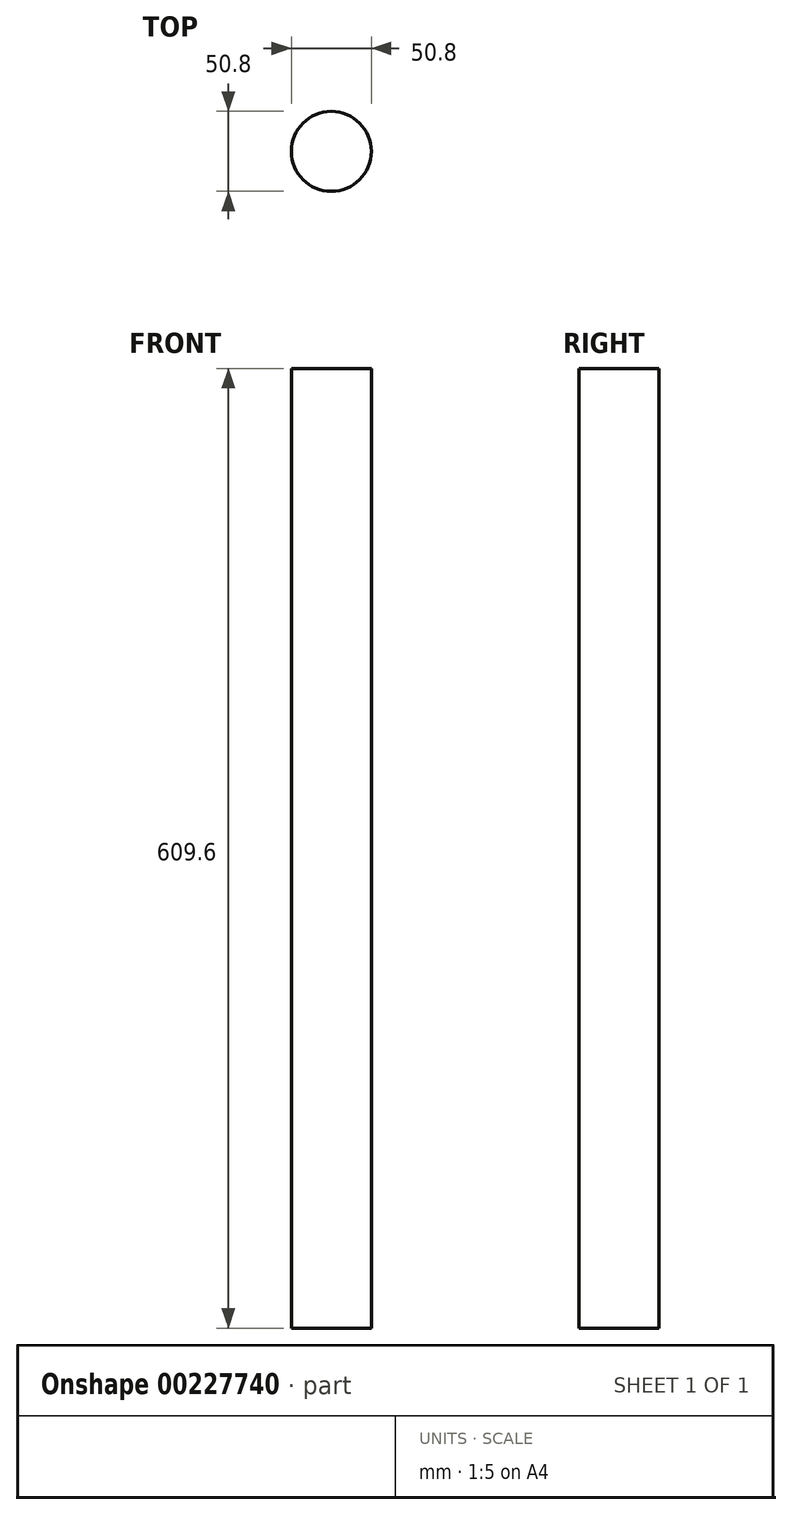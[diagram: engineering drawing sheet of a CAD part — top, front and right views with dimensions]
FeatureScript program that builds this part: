
annotation { "Feature Type Name" : "Feature", "Feature Type Description" : "" }
export const myFeature = defineFeature(function(context is Context, id is Id, definition is map)
    precondition{}
    {
        {
            var Q0;
            Q0=qCreatedBy(makeId("Top.planeOp"),FACE);
            var sketch = newSketch(context, id + "F0", { "sketchPlane" : qUnion([Q0])});
            skCircle(sketch, "E0", {"center": v(0, 0) * mm, "radius": 25.4 * mm});
            skSolve(sketch);
        }
        {
            var Q0;
            Q0 = qSketchRegion(id + "F0", true);
            var Q1;
            Q1=sQuery(id+"F0.wireOp",EDGE,"E0");
            extrude(context, id + "F1", {"entities" : qUnion([Q0]), "bodyType" : ToolBodyType.SURFACE, "surfaceEntities" : qUnion([Q1]), "depth" : 609.6 * mm});
        }
    });
